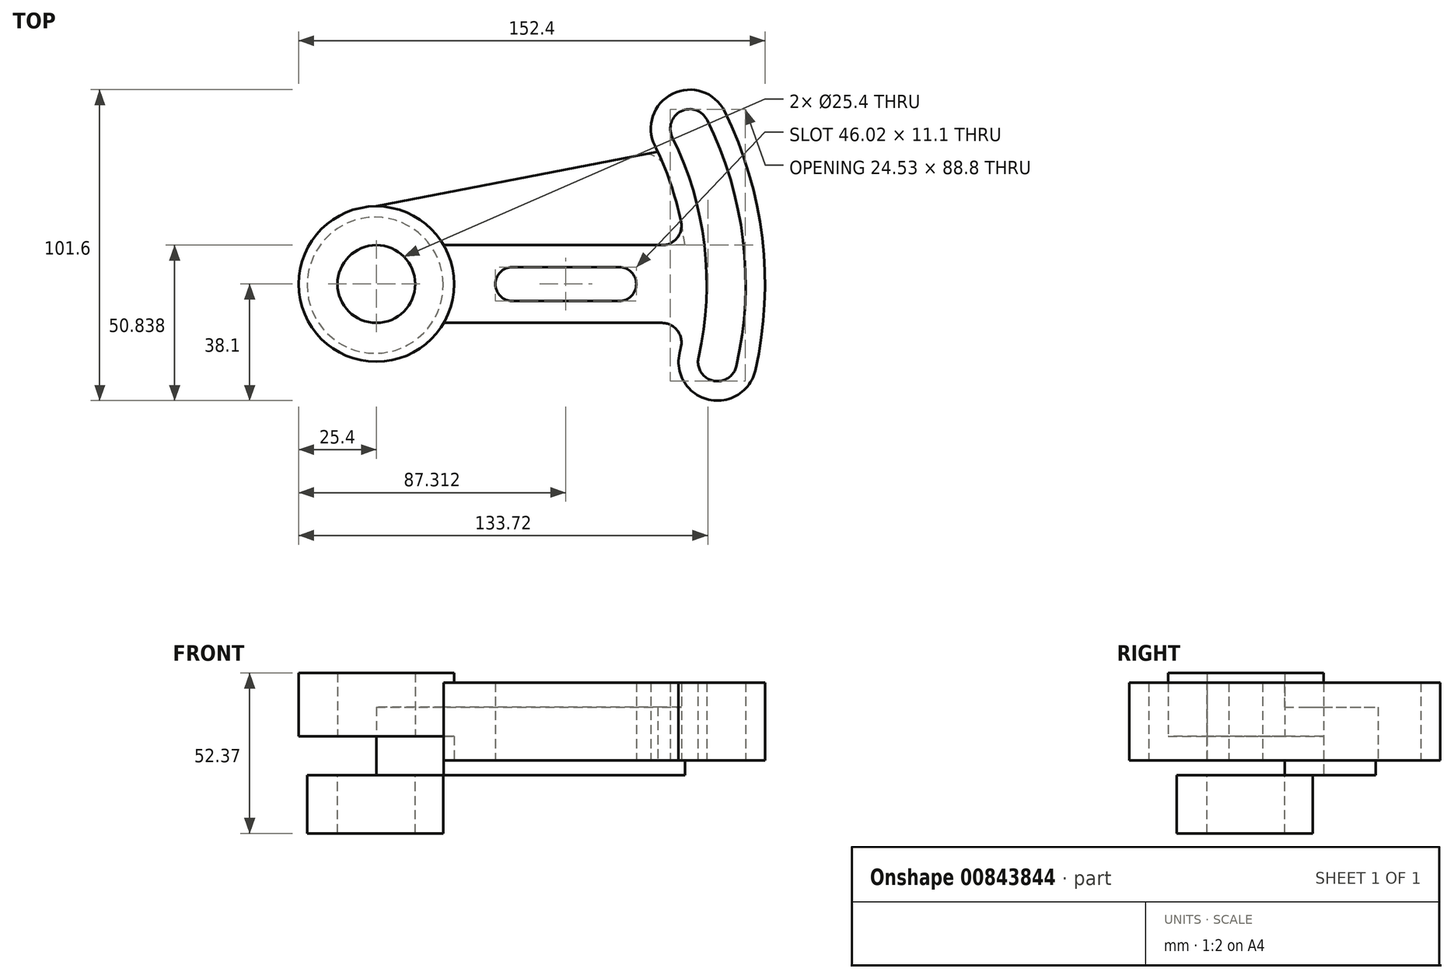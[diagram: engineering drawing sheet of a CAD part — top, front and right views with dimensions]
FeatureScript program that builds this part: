
annotation { "Feature Type Name" : "Feature", "Feature Type Description" : "" }
export const myFeature = defineFeature(function(context is Context, id is Id, definition is map)
    precondition{}
    {
        {
            var Q0;
            Q0=qCreatedBy(makeId("Top.planeOp"),FACE);
            var sketch = newSketch(context, id + "F0", { "sketchPlane" : qUnion([Q0])});
            skCircle(sketch, "E0", {"center": v(0, 0) * mm, "radius": 12.7 * mm});
            skCircle(sketch, "E1", {"center": v(-0.38, -0.38) * mm, "radius": 22.23 * mm});
            skCircle(sketch, "E2", {"center": v(0, 0) * mm, "radius": 25.4 * mm});
            skCircle(sketch, "E3", {"center": v(111.44, -25.4) * mm, "radius": 6.35 * mm});
            skCircle(sketch, "E4", {"center": v(102.4, 50.8) * mm, "radius": 6.35 * mm});
            skCircle(sketch, "E5", {"center": v(0, 0) * mm, "radius": 120.65 * mm});
            skCircle(sketch, "E6", {"center": v(0, 0) * mm, "radius": 107.95 * mm});
            skCircle(sketch, "E7", {"center": v(44.45, 0) * mm, "radius": 5.55 * mm});
            skCircle(sketch, "E8", {"center": v(79.38, 0) * mm, "radius": 5.55 * mm});
            skLineSegment(sketch, "E9", {"start": v(44.45, -5.55) * mm, "end": v(79.38, -5.55) * mm});
            skLineSegment(sketch, "E10", {"start": v(44.45, 5.55) * mm, "end": v(79.38, 5.55) * mm});
            skLineSegment(sketch, "E11", {"start": v(25.4, 12.7) * mm, "end": v(107.2, 12.7) * mm});
            skLineSegment(sketch, "E12", {"start": v(25.4, -12.7) * mm, "end": v(107.2, -12.7) * mm});
            skCircle(sketch, "E13", {"center": v(0, 0) * mm, "radius": 101.6 * mm});
            skCircle(sketch, "E14", {"center": v(0, 0) * mm, "radius": 127 * mm});
            skLineSegment(sketch, "E15", {"start": v(25.4, 12.7) * mm, "end": v(22, 12.7) * mm});
            skLineSegment(sketch, "E16", {"start": v(25.4, -12.7) * mm, "end": v(22, -12.7) * mm});
            skCircle(sketch, "E17", {"center": v(102.4, 50.8) * mm, "radius": 12.7 * mm});
            skCircle(sketch, "E18", {"center": v(111.44, -25.4) * mm, "radius": 12.7 * mm});
            skLineSegment(sketch, "E19", {"start": v(0, 0) * mm, "end": v(0, 25.4) * mm});
            skLineSegment(sketch, "E20", {"start": v(0, 25.4) * mm, "end": v(91.93, 43.27) * mm});
            skSolve(sketch);
        }
        {
            var Q0;
            Q0=makeQuery(id+"F0.imprint","IMPRINT",FACE,{"disambiguationData":[TD([[makeQuery(id+"F0.imprint","IMPRINT",EDGE,{"derivedFrom":sQuery(id+"F0.wireOp",EDGE,"E1")}),-1.0]])]});
            var Q1;
            Q1=makeQuery(id+"F0.imprint","IMPRINT",FACE,{"disambiguationData":[TD([[makeQuery(id+"F0.imprint","IMPRINT",EDGE,{"derivedFrom":sQuery(id+"F0.wireOp",EDGE,"E0")}),-1.0]])]});
            extrude(context, id + "F1", {"entities" : qUnion([Q0, Q1]), "depth" : 33.32 * mm, "offsetDistance" : 25.4 * mm});
        }
        {
            var Q0;
            Q0=makeQuery(id+"F0.imprint","IMPRINT",FACE,{"disambiguationData":[TD([[makeQuery(id+"F0.imprint","IMPRINT",EDGE,{"derivedFrom":sQuery(id+"F0.wireOp",EDGE,"E0")}),-1.0]])]});
            extrude(context, id + "F2", {"entities" : qUnion([Q0]), "oppositeDirection" : true, "depth" : 19.05 * mm, "offsetDistance" : 25.4 * mm});
        }
        {
            var Q0;
            {var subQ0=sQuery(id+"F0.wireOp",EDGE,"E9");Q0=makeQuery(id+"F0.imprint","IMPRINT",FACE,{"disambiguationData":[TD([[makeQuery(id+"F0.imprint","IMPRINT",EDGE,{"derivedFrom":subQ0}),-1.0]])]});}
            var Q1;
            {var subQ0=sQuery(id+"F0.wireOp",EDGE,"E11");var subQ1=sQuery(id+"F0.wireOp",EDGE,"E6");var subQ2=makeQuery(id+"F0.imprint","INTERSECT",VERTEX,{"derivedFrom":[subQ1,subQ0]});Q1=makeQuery(id+"F0.imprint","IMPRINT",FACE,{"disambiguationData":[TD([[makeQuery(id+"F0.imprint","IMPRINT",EDGE,{"disambiguationData":[TD([[subQ2,1.0]])],"derivedFrom":subQ1}),1.0]])]});}
            var Q2;
            {var subQ0=sQuery(id+"F0.wireOp",EDGE,"E11");var subQ1=sQuery(id+"F0.wireOp",EDGE,"E6");var subQ2=makeQuery(id+"F0.imprint","INTERSECT",VERTEX,{"derivedFrom":[subQ1,subQ0]});Q2=makeQuery(id+"F0.imprint","IMPRINT",FACE,{"disambiguationData":[TD([[makeQuery(id+"F0.imprint","IMPRINT",EDGE,{"disambiguationData":[TD([[subQ2,-1.0]])],"derivedFrom":subQ1}),1.0]])]});}
            var Q3;
            {var subQ0=sQuery(id+"F0.wireOp",EDGE,"E6");var subQ1=makeQuery(id+"F0.imprint","INTERSECT",VERTEX,{"derivedFrom":[sQuery(id+"F0.wireOp",EDGE,"E4"),subQ0]});Q3=makeQuery(id+"F0.imprint","IMPRINT",FACE,{"disambiguationData":[TD([[makeQuery(id+"F0.imprint","IMPRINT",EDGE,{"disambiguationData":[TD([[subQ1,1.0]])],"derivedFrom":subQ0}),1.0]])]});}
            var Q4;
            {var subQ0=sQuery(id+"F0.wireOp",EDGE,"E5");var subQ1=sQuery(id+"F0.wireOp",EDGE,"E4");var subQ2=makeQuery(id+"F0.imprint","INTERSECT",VERTEX,{"derivedFrom":[subQ1,subQ0]});Q4=makeQuery(id+"F0.imprint","IMPRINT",FACE,{"disambiguationData":[TD([[makeQuery(id+"F0.imprint","IMPRINT",EDGE,{"disambiguationData":[TD([[subQ2,-1.0]])],"derivedFrom":subQ1}),-1.0]])]});}
            var Q5;
            {var subQ0=sQuery(id+"F0.wireOp",EDGE,"E5");var subQ1=makeQuery(id+"F0.imprint","INTERSECT",VERTEX,{"derivedFrom":[sQuery(id+"F0.wireOp",EDGE,"E4"),subQ0]});Q5=makeQuery(id+"F0.imprint","IMPRINT",FACE,{"disambiguationData":[TD([[makeQuery(id+"F0.imprint","IMPRINT",EDGE,{"disambiguationData":[TD([[subQ1,1.0]])],"derivedFrom":subQ0}),-1.0]])]});}
            var Q6;
            {var subQ0=sQuery(id+"F0.wireOp",EDGE,"E17");var subQ1=sQuery(id+"F0.wireOp",EDGE,"E5");var subQ2=makeQuery(id+"F0.imprint","INTERSECT",VERTEX,{"disambiguationData":[OD(0.0)],"derivedFrom":[subQ1,subQ0]});Q6=makeQuery(id+"F0.imprint","IMPRINT",FACE,{"disambiguationData":[TD([[makeQuery(id+"F0.imprint","IMPRINT",EDGE,{"disambiguationData":[TD([[subQ2,1.0]])],"derivedFrom":subQ1}),-1.0]])]});}
            var Q7;
            {var subQ0=sQuery(id+"F0.wireOp",EDGE,"E5");var subQ1=makeQuery(id+"F0.imprint","INTERSECT",VERTEX,{"derivedFrom":[sQuery(id+"F0.wireOp",EDGE,"E3"),subQ0]});Q7=makeQuery(id+"F0.imprint","IMPRINT",FACE,{"disambiguationData":[TD([[makeQuery(id+"F0.imprint","IMPRINT",EDGE,{"disambiguationData":[TD([[subQ1,1.0]])],"derivedFrom":subQ0}),-1.0]])]});}
            var Q8;
            {var subQ0=sQuery(id+"F0.wireOp",EDGE,"E5");var subQ1=sQuery(id+"F0.wireOp",EDGE,"E3");var subQ2=makeQuery(id+"F0.imprint","INTERSECT",VERTEX,{"derivedFrom":[subQ1,subQ0]});Q8=makeQuery(id+"F0.imprint","IMPRINT",FACE,{"disambiguationData":[TD([[makeQuery(id+"F0.imprint","IMPRINT",EDGE,{"disambiguationData":[TD([[subQ2,1.0]])],"derivedFrom":subQ1}),-1.0]])]});}
            var Q9;
            {var subQ0=sQuery(id+"F0.wireOp",EDGE,"E6");var subQ1=makeQuery(id+"F0.imprint","INTERSECT",VERTEX,{"derivedFrom":[sQuery(id+"F0.wireOp",EDGE,"E3"),subQ0]});Q9=makeQuery(id+"F0.imprint","IMPRINT",FACE,{"disambiguationData":[TD([[makeQuery(id+"F0.imprint","IMPRINT",EDGE,{"disambiguationData":[TD([[subQ1,1.0]])],"derivedFrom":subQ0}),1.0]])]});}
            var Q10;
            {var subQ0=sQuery(id+"F0.wireOp",EDGE,"E12");var subQ1=sQuery(id+"F0.wireOp",EDGE,"E6");var subQ2=makeQuery(id+"F0.imprint","INTERSECT",VERTEX,{"derivedFrom":[subQ1,subQ0]});Q10=makeQuery(id+"F0.imprint","IMPRINT",FACE,{"disambiguationData":[TD([[makeQuery(id+"F0.imprint","IMPRINT",EDGE,{"disambiguationData":[TD([[subQ2,1.0]])],"derivedFrom":subQ1}),1.0]])]});}
            extrude(context, id + "F3", {"entities" : qUnion([Q0, Q1, Q2, Q3, Q4, Q5, Q6, Q7, Q8, Q9, Q10]), "operationType" : NewBodyOperationType.ADD, "depth" : 30.15 * mm, "offsetDistance" : 25.4 * mm});
        }
        {
            var Q0;
            {var subQ0=sQuery(id+"F0.wireOp",EDGE,"E2");Q0=makeQuery(id+"F3.boolean.opBoolean","MERGE",FACE,{"derivedFrom":[makeQuery(id+"F1.opExtrude","CAP_FACE",FACE,{"disambiguationData":[OSD([sQuery(id+"F0.wireOp",EDGE,"E0"),subQ0])],"isStart":true}),makeQuery(id+"F3.opExtrude","CAP_FACE",FACE,{"disambiguationData":[OSD([subQ0,sQuery(id+"F0.wireOp",EDGE,"E3"),sQuery(id+"F0.wireOp",EDGE,"E4"),sQuery(id+"F0.wireOp",EDGE,"E5"),sQuery(id+"F0.wireOp",EDGE,"E6"),sQuery(id+"F0.wireOp",EDGE,"E7"),sQuery(id+"F0.wireOp",EDGE,"E8"),sQuery(id+"F0.wireOp",EDGE,"E9"),sQuery(id+"F0.wireOp",EDGE,"E10"),sQuery(id+"F0.wireOp",EDGE,"E11"),sQuery(id+"F0.wireOp",EDGE,"E12"),sQuery(id+"F0.wireOp",EDGE,"E13"),sQuery(id+"F0.wireOp",EDGE,"E14"),sQuery(id+"F0.wireOp",EDGE,"E15"),sQuery(id+"F0.wireOp",EDGE,"E16"),sQuery(id+"F0.wireOp",EDGE,"E17"),sQuery(id+"F0.wireOp",EDGE,"E18")])],"isStart":true})]});}
            var sketch = newSketch(context, id + "F4", { "sketchPlane" : qUnion([Q0])});
            skCircle(sketch, "E21", {"center": v(0, 0) * mm, "radius": 25.4 * mm});
            skSolve(sketch);
        }
        {
            var Q0;
            Q0=makeQuery(id+"F4.imprint","IMPRINT",FACE,{"disambiguationData":[TD([[makeQuery(id+"F4.imprint","IMPRINT",EDGE,{"disambiguationData":[OD(1.0)],"derivedFrom":sQuery(id+"F4.wireOp",EDGE,"E21")}),-1.0]])]});
            extrude(context, id + "F5", {"entities" : qUnion([Q0]), "operationType" : NewBodyOperationType.REMOVE, "oppositeDirection" : true, "depth" : 4.75 * mm, "offsetDistance" : 25.4 * mm});
        }
        {
            var Q0;
            {var subQ0=sQuery(id+"F0.wireOp",EDGE,"E15");Q0=makeQuery(id+"F0.imprint","IMPRINT",FACE,{"disambiguationData":[TD([[makeQuery(id+"F0.imprint","IMPRINT",EDGE,{"derivedFrom":subQ0}),-1.0]])]});}
            extrude(context, id + "F6", {"entities" : qUnion([Q0]), "operationType" : NewBodyOperationType.ADD, "depth" : 22.22 * mm, "offsetDistance" : 25.4 * mm});
        }
        {
            var Q0;
            {var subQ0=sQuery(id+"F0.wireOp",EDGE,"E15");var subQ1=sQuery(id+"F0.wireOp",EDGE,"E13");var subQ2=sQuery(id+"F0.wireOp",EDGE,"E11");var subQ3=sQuery(id+"F0.wireOp",EDGE,"E2");Q0=makeQuery(id+"F6.boolean.opBoolean","MERGE",FACE,{"derivedFrom":[makeQuery(id+"F3.boolean.opBoolean","MERGE",FACE,{"derivedFrom":[makeQuery(id+"F1.opExtrude","CAP_FACE",FACE,{"disambiguationData":[OSD([sQuery(id+"F0.wireOp",EDGE,"E0"),subQ3])],"isStart":true}),makeQuery(id+"F3.opExtrude","CAP_FACE",FACE,{"disambiguationData":[OSD([subQ3,sQuery(id+"F0.wireOp",EDGE,"E3"),sQuery(id+"F0.wireOp",EDGE,"E4"),sQuery(id+"F0.wireOp",EDGE,"E5"),sQuery(id+"F0.wireOp",EDGE,"E6"),sQuery(id+"F0.wireOp",EDGE,"E7"),sQuery(id+"F0.wireOp",EDGE,"E8"),sQuery(id+"F0.wireOp",EDGE,"E9"),sQuery(id+"F0.wireOp",EDGE,"E10"),subQ2,sQuery(id+"F0.wireOp",EDGE,"E12"),subQ1,sQuery(id+"F0.wireOp",EDGE,"E14"),subQ0,sQuery(id+"F0.wireOp",EDGE,"E16"),sQuery(id+"F0.wireOp",EDGE,"E17"),sQuery(id+"F0.wireOp",EDGE,"E18")])],"isStart":true})]}),makeQuery(id+"F6.opExtrude","CAP_FACE",FACE,{"disambiguationData":[OSD([subQ3,subQ2,subQ1,subQ0,sQuery(id+"F0.wireOp",EDGE,"E20")])],"isStart":true})]});}
            var sketch = newSketch(context, id + "F7", { "sketchPlane" : qUnion([Q0])});
            skCircle(sketch, "E22", {"center": v(0, 0) * mm, "radius": 25.4 * mm});
            skSolve(sketch);
        }
        {
            var Q0;
            Q0=makeQuery(id+"F7.imprint","IMPRINT",FACE,{"disambiguationData":[TD([[makeQuery(id+"F7.imprint","IMPRINT",EDGE,{"disambiguationData":[OD(1.0)],"derivedFrom":sQuery(id+"F7.wireOp",EDGE,"E22")}),-1.0]])]});
            extrude(context, id + "F8", {"entities" : qUnion([Q0]), "operationType" : NewBodyOperationType.REMOVE, "oppositeDirection" : true, "depth" : 12.7 * mm, "offsetDistance" : 25.4 * mm});
        }
        {
            var Q0;
            Q0=makeQuery(id+"F8.boolean.opBoolean","COPY",EDGE,{"derivedFrom":makeQuery(id+"F8.opExtrude","SWEPT_EDGE",EDGE,{"disambiguationData":[OSD([sQuery(id+"F0.wireOp",EDGE,"E11"),sQuery(id+"F0.wireOp",EDGE,"E13"),sQuery(id+"F0.wireOp",EDGE,"E15")])]})});
            var Q1;
            Q1=makeQuery(id+"F3.opExtrude","SWEPT_EDGE",EDGE,{"disambiguationData":[OSD([sQuery(id+"F0.wireOp",EDGE,"E11"),sQuery(id+"F0.wireOp",EDGE,"E13")])]});
            var Q2;
            {var subQ0=sQuery(id+"F0.wireOp",EDGE,"E20");var subQ1=sQuery(id+"F0.wireOp",EDGE,"E13");var subQ2=makeQuery(id+"F0.imprint","INTERSECT",VERTEX,{"derivedFrom":[subQ1,subQ0]});Q2=makeQuery(id+"F6.boolean.opBoolean","SPLIT",EDGE,{"disambiguationData":[topologyDisambiguationEdgeConnected([makeQuery(id+"F3.opExtrude","SWEPT_FACE",FACE,{"disambiguationData":[OSD([subQ1]),TDD([makeQuery(id+"F0.imprint","IMPRINT",EDGE,{"disambiguationData":[TD([[subQ2,1.0]])],"derivedFrom":subQ1}),makeQuery(id+"F0.imprint","IMPRINT",EDGE,{"disambiguationData":[TD([[subQ2,-1.0]])],"derivedFrom":subQ1})])]})])],"derivedFrom":makeQuery(id+"F6.opExtrude","SWEPT_EDGE",EDGE,{"disambiguationData":[OSD([subQ1,subQ0])]})});}
            var Q3;
            Q3=makeQuery(id+"F3.opExtrude","SWEPT_EDGE",EDGE,{"disambiguationData":[OSD([sQuery(id+"F0.wireOp",EDGE,"E12"),sQuery(id+"F0.wireOp",EDGE,"E13")])]});
            fillet(context, id + "F9", {"entities" : qUnion([Q0, Q1, Q2, Q3]), "radius" : 6.35 * mm, "tangentPropagation" : true, "allowEdgeOverflow" : false});
        }
    });
